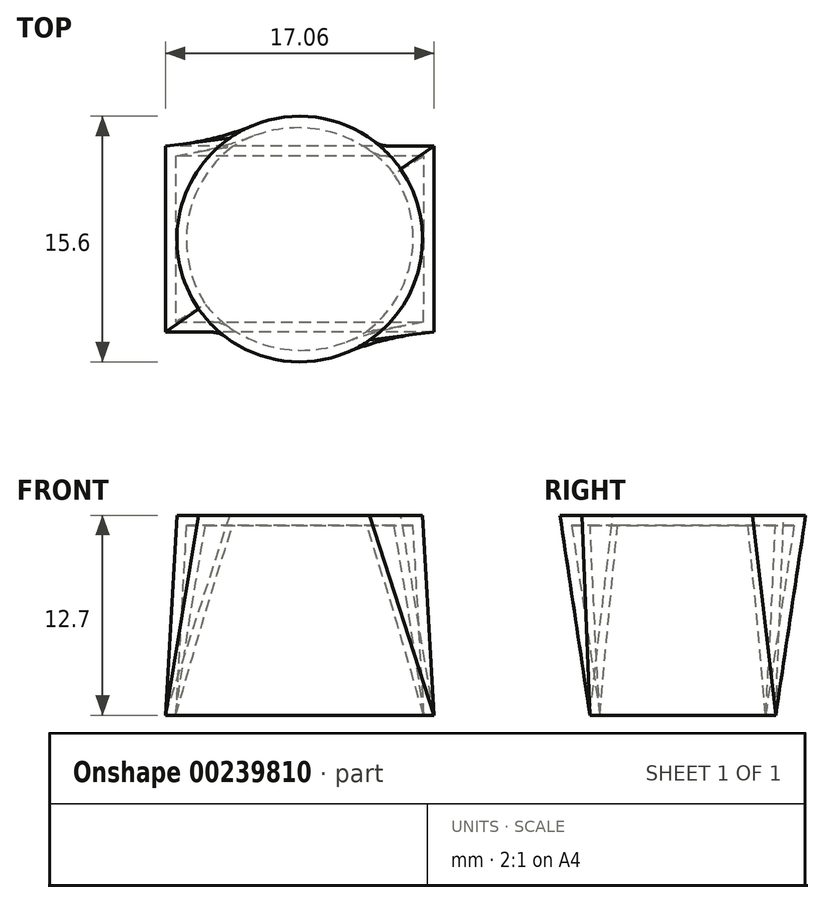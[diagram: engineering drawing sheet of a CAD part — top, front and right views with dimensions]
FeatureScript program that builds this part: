
annotation { "Feature Type Name" : "Feature", "Feature Type Description" : "" }
export const myFeature = defineFeature(function(context is Context, id is Id, definition is map)
    precondition{}
    {
        {
            var Q0;
            Q0=qCreatedBy(makeId("Top.planeOp"),FACE);
            cPlane(context, id + "F0", {"entities" : qUnion([Q0]), "cplaneType" : CPlaneType.OFFSET, "offset" : 50.8 * mm, "width" : 152.4 * mm, "height" : 152.4 * mm});
        }
        {
            var Q0;
            Q0=qCreatedBy(id+"F0.planeOp",FACE);
            var sketch = newSketch(context, id + "F1", { "sketchPlane" : qUnion([Q0])});
            skCircle(sketch, "E0", {"center": v(0, 0) * mm, "radius": 31.21 * mm});
            skSolve(sketch);
        }
        {
            var Q0;
            Q0=qCreatedBy(makeId("Top.planeOp"),FACE);
            var sketch = newSketch(context, id + "F2", { "sketchPlane" : qUnion([Q0])});
            skLineSegment(sketch, "E1.bottom", {"start": v(34.12, 23.6) * mm, "end": v(-34.12, 23.6) * mm});
            skLineSegment(sketch, "E1.top", {"start": v(34.12, -23.6) * mm, "end": v(-34.12, -23.6) * mm});
            skLineSegment(sketch, "E1.left", {"start": v(34.12, 23.6) * mm, "end": v(34.12, -23.6) * mm});
            skLineSegment(sketch, "E1.right", {"start": v(-34.12, 23.6) * mm, "end": v(-34.12, -23.6) * mm});
            skPoint(sketch, "E1.middle", {"position": v(0, 0) * mm});
            skSolve(sketch);
        }
        {
            var Q0;
            Q0=makeQuery(id+"F2.imprint","IMPRINT",FACE,{"disambiguationData":[TD([[makeQuery(id+"F2.imprint","IMPRINT",EDGE,{"derivedFrom":sQuery(id+"F2.wireOp",EDGE,"E1.bottom")}),1.0]])]});
            var Q1;
            Q1=makeQuery(id+"F1.imprint","IMPRINT",FACE,{"disambiguationData":[TD([[makeQuery(id+"F1.imprint","IMPRINT",EDGE,{"derivedFrom":sQuery(id+"F1.wireOp",EDGE,"E0")}),1.0]])]});
            loft(context, id + "F3", {"sheetProfilesArray" : [{ "sheetProfileEntities" : qUnion([Q0]) }, { "sheetProfileEntities" : qUnion([Q1]) }]});
        }
        {
            var Q0;
            Q0=makeQuery(id+"F3.opLoft","CAP_FACE",FACE,{"disambiguationData":[OSD([makeQuery(id+"F2.imprint","IMPRINT",FACE,{"disambiguationData":[TD([[makeQuery(id+"F2.imprint","IMPRINT",EDGE,{"derivedFrom":sQuery(id+"F2.wireOp",EDGE,"E1.bottom")}),1.0]])]})])],"isStart":true});
            shell(context, id + "F4", {"entities" : qUnion([Q0]), "thickness" : 2.54 * mm});
        }
        {
            var Q0;
            Q0=makeQuery(id+"F3.opLoft","SWEPT_BODY",BODY,{"disambiguationData":[OSD([makeQuery(id+"F1.imprint","IMPRINT",FACE,{"disambiguationData":[TD([[makeQuery(id+"F1.imprint","IMPRINT",EDGE,{"derivedFrom":sQuery(id+"F1.wireOp",EDGE,"E0")}),1.0]])]}),makeQuery(id+"F2.imprint","IMPRINT",FACE,{"disambiguationData":[TD([[makeQuery(id+"F2.imprint","IMPRINT",EDGE,{"derivedFrom":sQuery(id+"F2.wireOp",EDGE,"E1.bottom")}),1.0]])]})])]});
            var Q1;
            Q1=qCreatedBy(makeId("Origin.pointOp"),VERTEX);
            transform(context, id + "F5", {"entities" : qUnion([Q0]), "transformType" : TransformType.SCALE_UNIFORMLY, "scale" : .25, "scalePoint" : qUnion([Q1]), "makeCopy" : false});
        }
    });
